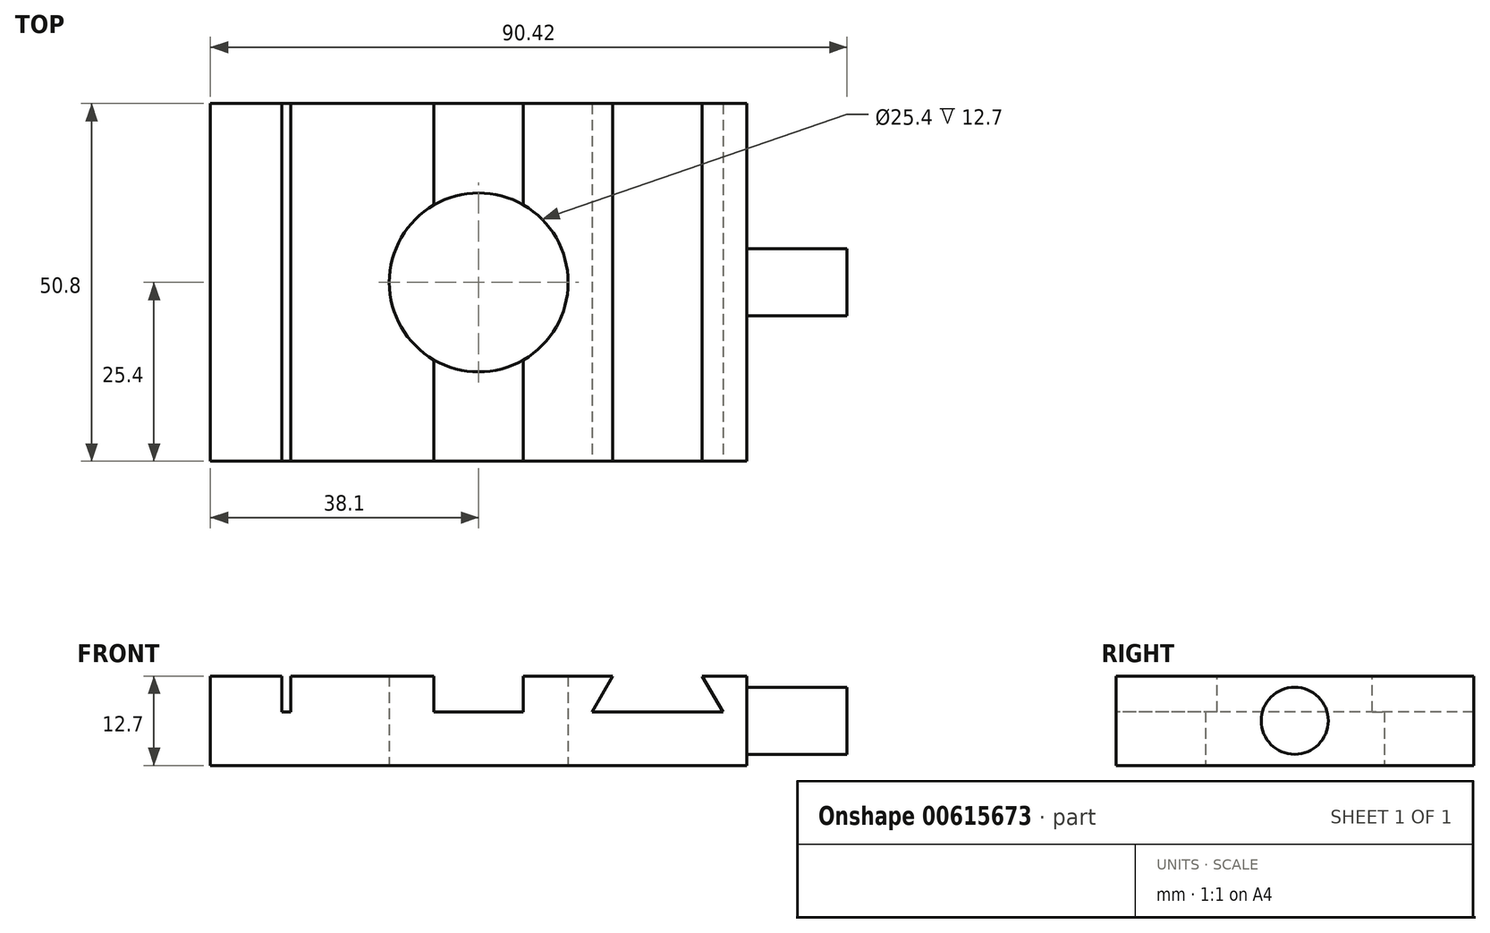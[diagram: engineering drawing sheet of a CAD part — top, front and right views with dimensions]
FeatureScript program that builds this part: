
annotation { "Feature Type Name" : "Feature", "Feature Type Description" : "" }
export const myFeature = defineFeature(function(context is Context, id is Id, definition is map)
    precondition{}
    {
        {
            var Q0;
            Q0=qCreatedBy(makeId("Top.planeOp"),FACE);
            var sketch = newSketch(context, id + "F0", { "sketchPlane" : qUnion([Q0])});
            skLineSegment(sketch, "E0.bottom", {"start": v(-38.1, 25.4) * mm, "end": v(38.1, 25.4) * mm});
            skLineSegment(sketch, "E0.top", {"start": v(-38.1, -25.4) * mm, "end": v(38.1, -25.4) * mm});
            skLineSegment(sketch, "E0.left", {"start": v(-38.1, 25.4) * mm, "end": v(-38.1, -25.4) * mm});
            skLineSegment(sketch, "E0.right", {"start": v(38.1, 25.4) * mm, "end": v(38.1, -25.4) * mm});
            skPoint(sketch, "E0.middle", {"position": v(0, 0) * mm});
            skCircle(sketch, "E1", {"center": v(0, 0) * mm, "radius": 12.7 * mm});
            skSolve(sketch);
        }
        {
            var Q0;
            Q0=makeQuery(id+"F0.imprint","IMPRINT",FACE,{"disambiguationData":[TD([[makeQuery(id+"F0.imprint","IMPRINT",EDGE,{"derivedFrom":sQuery(id+"F0.wireOp",EDGE,"E0.bottom")}),-1.0]])]});
            extrude(context, id + "F1", {"entities" : qUnion([Q0]), "depth" : 12.7 * mm, "offsetDistance" : 25.4 * mm});
        }
        {
            var Q0;
            Q0=makeQuery(id+"F1.opExtrude","CAP_FACE",FACE,{"disambiguationData":[OSD([sQuery(id+"F0.wireOp",EDGE,"E0.bottom"),sQuery(id+"F0.wireOp",EDGE,"E0.top"),sQuery(id+"F0.wireOp",EDGE,"E0.left"),sQuery(id+"F0.wireOp",EDGE,"E0.right"),sQuery(id+"F0.wireOp",EDGE,"E1")])],"isStart":false});
            var sketch = newSketch(context, id + "F2", { "sketchPlane" : qUnion([Q0])});
            skLineSegment(sketch, "E2.bottom", {"start": v(-27.94, 25.4) * mm, "end": v(-26.67, 25.4) * mm});
            skLineSegment(sketch, "E2.top", {"start": v(-27.94, -25.4) * mm, "end": v(-26.67, -25.4) * mm});
            skLineSegment(sketch, "E2.left", {"start": v(-27.94, 25.4) * mm, "end": v(-27.94, -25.4) * mm});
            skLineSegment(sketch, "E2.right", {"start": v(-26.67, 25.4) * mm, "end": v(-26.67, -25.4) * mm});
            skLineSegment(sketch, "E3", {"start": v(-6.35, 25.4) * mm, "end": v(-6.35, -25.4) * mm});
            skLineSegment(sketch, "E4", {"start": v(-6.35, -25.4) * mm, "end": v(6.35, -25.4) * mm});
            skLineSegment(sketch, "E5", {"start": v(6.35, -25.4) * mm, "end": v(6.35, 25.4) * mm});
            skLineSegment(sketch, "E6", {"start": v(6.35, 25.4) * mm, "end": v(-6.35, 25.4) * mm});
            skLineSegment(sketch, "E7", {"start": v(-38.1, 25.4) * mm, "end": v(0, 25.4) * mm, "construction": true});
            skLineSegment(sketch, "E8", {"start": v(0, 25.4) * mm, "end": v(0, -25.4) * mm, "construction": true});
            skSolve(sketch);
        }
        {
            var Q0;
            Q0=makeQuery(id+"F2.imprint","IMPRINT",FACE,{"disambiguationData":[TD([[makeQuery(id+"F2.imprint","IMPRINT",EDGE,{"derivedFrom":sQuery(id+"F2.wireOp",EDGE,"E2.bottom")}),-1.0]])]});
            var Q1;
            {var subQ0=sQuery(id+"F2.wireOp",EDGE,"E4");Q1=makeQuery(id+"F2.imprint","IMPRINT",FACE,{"disambiguationData":[TD([[makeQuery(id+"F2.imprint","IMPRINT",EDGE,{"derivedFrom":subQ0}),1.0]])]});}
            var Q2;
            {var subQ0=sQuery(id+"F2.wireOp",EDGE,"E6");Q2=makeQuery(id+"F2.imprint","IMPRINT",FACE,{"disambiguationData":[TD([[makeQuery(id+"F2.imprint","IMPRINT",EDGE,{"derivedFrom":subQ0}),-1.0]])]});}
            extrude(context, id + "F3", {"entities" : qUnion([Q0, Q1, Q2]), "operationType" : NewBodyOperationType.REMOVE, "oppositeDirection" : true, "depth" : 5.08 * mm, "offsetDistance" : 25.4 * mm});
        }
        {
            var Q0;
            Q0=makeQuery(id+"F1.opExtrude","SWEPT_FACE",FACE,{"disambiguationData":[OSD([sQuery(id+"F0.wireOp",EDGE,"E0.top")])]});
            var sketch = newSketch(context, id + "F4", { "sketchPlane" : qUnion([Q0])});
            skLineSegment(sketch, "E9", {"start": v(19.05, 12.7) * mm, "end": v(16.12, 7.62) * mm});
            skLineSegment(sketch, "E10", {"start": v(16.12, 7.62) * mm, "end": v(34.68, 7.62) * mm});
            skLineSegment(sketch, "E11", {"start": v(34.68, 7.62) * mm, "end": v(31.75, 12.7) * mm});
            skLineSegment(sketch, "E12", {"start": v(31.75, 12.7) * mm, "end": v(19.05, 12.7) * mm});
            skLineSegment(sketch, "E13", {"start": v(25.4, 7.62) * mm, "end": v(25.4, 12.7) * mm, "construction": true});
            skSolve(sketch);
        }
        {
            var Q0;
            Q0=makeQuery(id+"F4.imprint","IMPRINT",FACE,{"disambiguationData":[TD([[makeQuery(id+"F4.imprint","IMPRINT",EDGE,{"derivedFrom":sQuery(id+"F4.wireOp",EDGE,"E9")}),1.0]])]});
            extrude(context, id + "F5", {"entities" : qUnion([Q0]), "operationType" : NewBodyOperationType.REMOVE, "endBound" : BoundingType.THROUGH_ALL, "oppositeDirection" : true, "depth" : 25.4 * mm, "offsetDistance" : 25.4 * mm});
        }
        {
            var Q0;
            Q0=makeQuery(id+"F1.opExtrude","SWEPT_FACE",FACE,{"disambiguationData":[OSD([sQuery(id+"F0.wireOp",EDGE,"E0.right")])]});
            var sketch = newSketch(context, id + "F6", { "sketchPlane" : qUnion([Q0])});
            skCircle(sketch, "E14", {"center": v(0, 6.35) * mm, "radius": 4.76 * mm});
            skPoint(sketch, "E14.centerSnap0", {"position": v(-25.4, 6.35) * mm});
            skPoint(sketch, "E14.centerSnap1", {"position": v(0, 12.7) * mm});
            skSolve(sketch);
        }
        {
            var Q0;
            Q0=makeQuery(id+"F6.imprint","IMPRINT",FACE,{"disambiguationData":[TD([[makeQuery(id+"F6.imprint","IMPRINT",EDGE,{"derivedFrom":sQuery(id+"F6.wireOp",EDGE,"E14")}),1.0]])]});
            extrude(context, id + "F7", {"entities" : qUnion([Q0]), "operationType" : NewBodyOperationType.ADD, "depth" : 14.22 * mm, "offsetDistance" : 25.4 * mm});
        }
    });
